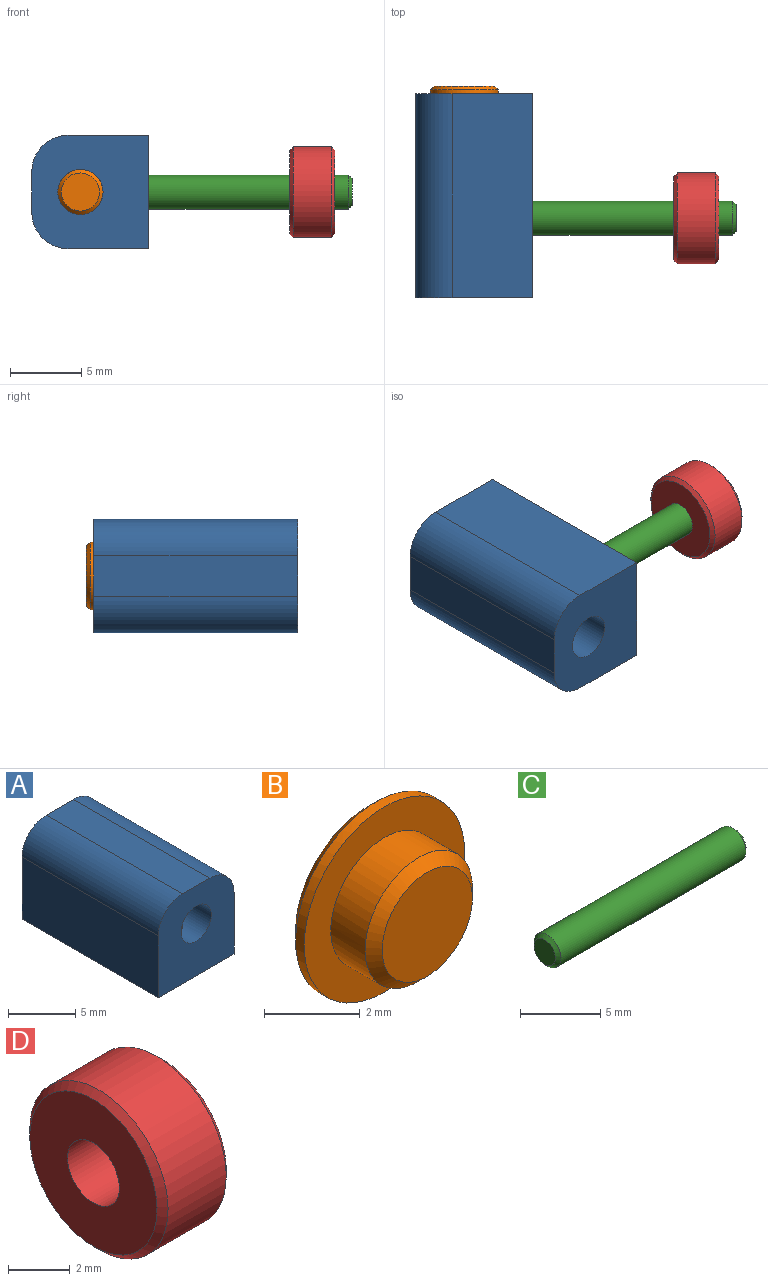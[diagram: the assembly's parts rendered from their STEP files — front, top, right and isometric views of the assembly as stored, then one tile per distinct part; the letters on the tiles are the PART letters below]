
ASSEMBLY  parts=4 mates=3
PART A: 12 faces, bbox 7.9x14.3x8.2 mm
  f0: cylinder r=1.59mm len=14.29mm, axis (0,-1,0), area 141.1mm2, adj f5,f6,f11
  f1: plane 14.29x2.86mm, normal (0,0,1), area 40.8mm2, adj f5,f6,f7,f8
  f2: plane 14.29x5.63mm, normal (-1,0,0), area 80.4mm2, adj f3,f5,f6,f7
  f3: plane 14.29x7.94mm, normal (0,0,-1), area 107.6mm2, adj f2,f4,f5,f6,f9,f11
  f4: plane 14.29x5.63mm, normal (1,0,0), area 80.4mm2, adj f3,f5,f6,f8
  f5: plane 8.17x7.94mm, normal (0,1,0), area 54.1mm2, adj f0,f1,f2,f3,f4,f7,f8
  f6: plane 8.17x7.94mm, normal (0,-1,0), area 54.1mm2, adj f0,f1,f2,f3,f4,f7,f8
  f7: cylinder r=2.54mm len=14.29mm, axis (0,-1,0), area 57mm2, adj f1,f2,f5,f6
  f8: cylinder r=2.54mm len=14.29mm, axis (0,1,0), area 57mm2, adj f1,f4,f5,f6
  f9: cylinder r=1.19mm len=2.54mm, axis (0,0,-1), area 19mm2, adj f3,f10
  f10: plane 2.38x2.38mm, normal (0,0,-1), area 4.5mm2, adj f9
  f11: cylinder r=0.66mm len=3.32mm, axis (0,0,-1), area 13.5mm2, adj f0,f3
PART B: 7 faces, bbox 4.8x1.8x4.8 mm
  f0: cylinder r=1.59mm len=3.18mm, axis (0,1,0), area 10.1mm2, adj f3,f5
  f1: plane 2.67x2.67mm, normal (0,-1,0), area 5.6mm2, adj f5
  f2: cylinder r=2.37mm len=4.75mm, axis (0,-1,0), area 3.8mm2, adj f3,f6
  f3: plane 4.75x4.75mm, normal (0,-1,0), area 9.8mm2, adj f0,f2
  f4: plane 4.24x4.24mm, normal (0,1,0), area 14.1mm2, adj f6
  f5: cone r=1.33mm half-angle=45deg, axis (0,1,0), area 3.3mm2, adj f0,f1
  f6: cone r=2.37mm half-angle=45deg, axis (0,-1,0), area 5.1mm2, adj f2,f4
PART C: 5 faces, bbox 16.8x2.4x2.4 mm
  f0: cylinder r=1.19mm len=16.31mm, axis (-1,0,0), area 122.1mm2, adj f3,f4
  f1: plane 1.87x1.87mm, normal (1,0,0), area 2.8mm2, adj f4
  f2: plane 1.87x1.87mm, normal (-1,0,0), area 2.8mm2, adj f3
  f3: cone r=1.19mm half-angle=45deg, axis (1,0,0), area 2.4mm2, adj f0,f2
  f4: cone r=0.94mm half-angle=45deg, axis (-1,0,0), area 2.4mm2, adj f0,f1
PART D: 6 faces, bbox 3.2x6.4x6.4 mm
  f0: cylinder r=1.19mm len=3.18mm, axis (-1,0,0), area 23.8mm2, adj f2,f3
  f1: cylinder r=3.17mm len=6.35mm, axis (-1,0,0), area 53.2mm2, adj f4,f5
  f2: plane 5.84x5.84mm, normal (1,0,0), area 22.3mm2, adj f0,f5
  f3: plane 5.84x5.84mm, normal (-1,0,0), area 22.3mm2, adj f0,f4
  f4: cone r=3.17mm half-angle=45deg, axis (1,0,0), area 6.9mm2, adj f1,f3
  f5: cone r=2.92mm half-angle=45deg, axis (-1,0,0), area 6.9mm2, adj f1,f2
PLACE A rot(axis=(0.71,0,-0.71),180deg) t=(3.29,17.63,2.16)mm
PLACE B rot(axis=(0,1,0),90deg) t=(-1.47,17.63,-1.81)mm
PLACE C t=(0.75,8.9,-1.81)mm
PLACE D t=(13.18,8.9,-1.81)mm
MATE fastened A.f9 <-> C.f0  axis (1,0,0) through (0.75,8.9,-1.81)mm
MATE fastened D.f0 <-> C.f0  axis (-1,0,0) through (14.77,8.9,-1.81)mm
MATE fastened B.f0 <-> A.f0  axis (0,1,0) through (-1.47,17.63,-1.81)mm
